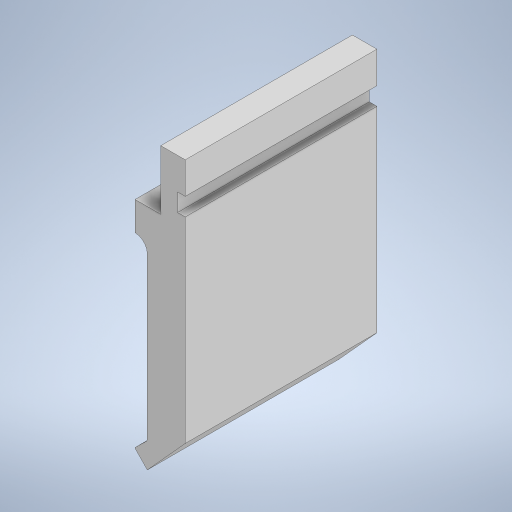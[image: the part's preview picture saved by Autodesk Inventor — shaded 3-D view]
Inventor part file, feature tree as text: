
AUTODESK INVENTOR PART (.ipt)
format: ipt  version: 2023.1 (Build 271208000, 208)  size: 260,608 bytes
history: native  units: mm
features: extrude x1
ambient origin geometry x8: Origin, YZ Plane, XZ Plane, XY Plane, X Axis, Y Axis, Z Axis, Center Point
bodies: Solid1 (feature_tree)
feature tree (1):
  extrude  "Extrusion1"  Depth=150.0mm
